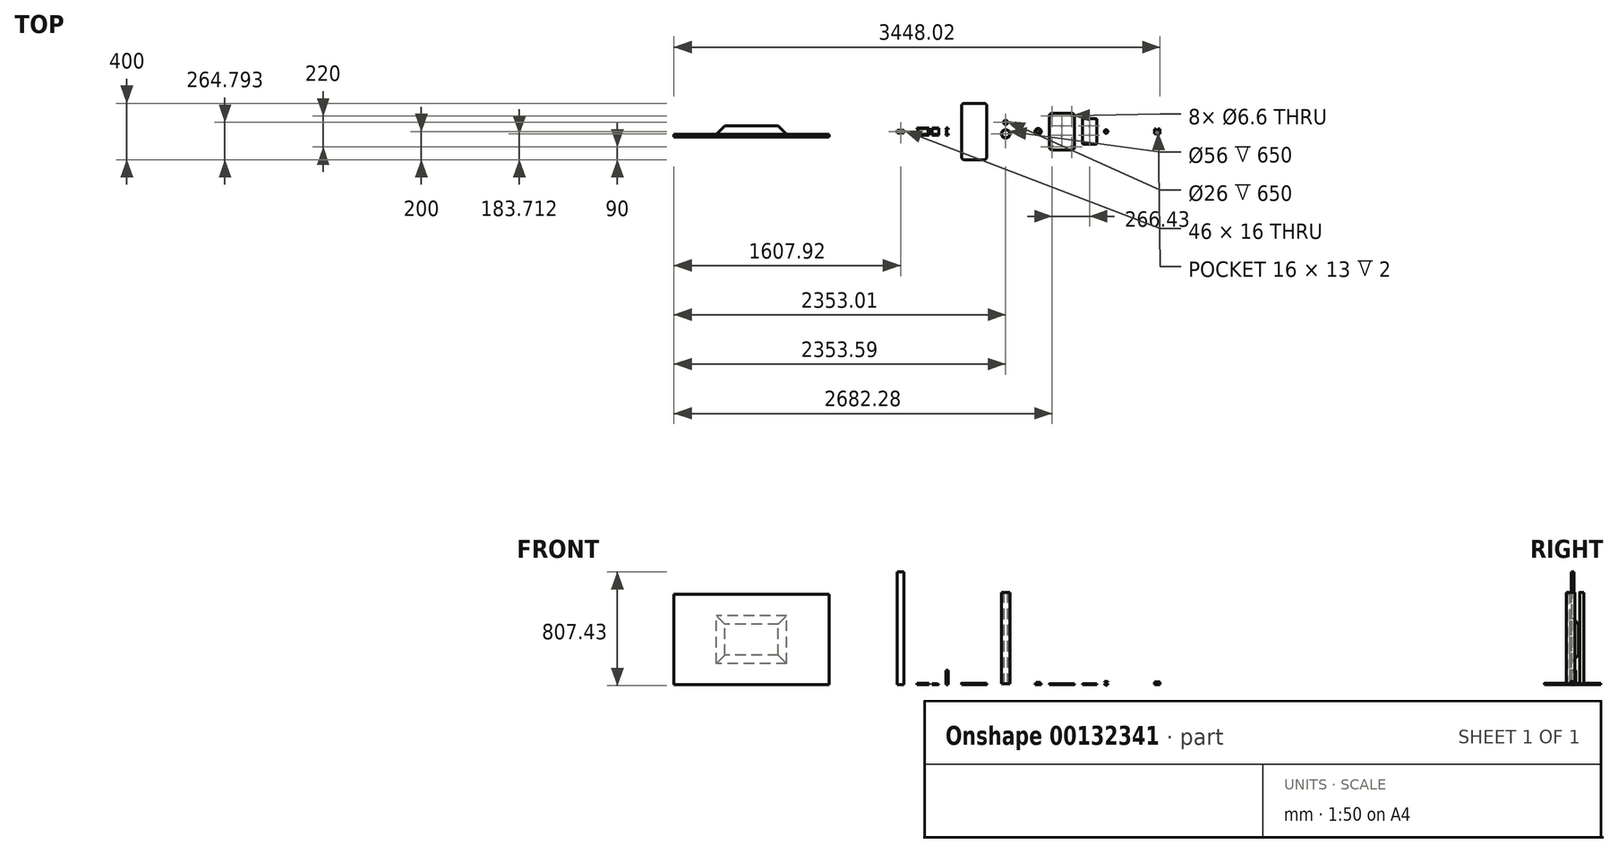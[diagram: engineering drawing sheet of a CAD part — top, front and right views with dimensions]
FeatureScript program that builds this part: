
annotation { "Feature Type Name" : "Feature", "Feature Type Description" : "" }
export const myFeature = defineFeature(function(context is Context, id is Id, definition is map)
    precondition{}
    {
        {
            var Q0;
            Q0=qCreatedBy(makeId("Top.planeOp"),FACE);
            var sketch = newSketch(context, id + "F0", { "sketchPlane" : qUnion([Q0])});
            skLineSegment(sketch, "E0.bottom", {"start": v(78.82, 130) * mm, "end": v(258.82, 130) * mm});
            skLineSegment(sketch, "E0.top", {"start": v(78.82, -130) * mm, "end": v(258.82, -130) * mm});
            skLineSegment(sketch, "E0.left", {"start": v(78.82, 130) * mm, "end": v(78.82, -130) * mm});
            skLineSegment(sketch, "E0.right", {"start": v(258.82, 130) * mm, "end": v(258.82, -130) * mm});
            skPoint(sketch, "E0.middle", {"position": v(0, 0) * mm});
            skSolve(sketch);
        }
        {
            var Q0;
            Q0 = qSketchRegion(id + "F0", true);
            extrude(context, id + "F1", {"entities" : qUnion([Q0]), "depth" : 5 * mm});
        }
        {
            var Q0;
            Q0=makeQuery(id+"F1.opExtrude","CAP_FACE",FACE,{"disambiguationData":[OSD([sQuery(id+"F0.wireOp",EDGE,"E0.bottom"),sQuery(id+"F0.wireOp",EDGE,"E0.top"),sQuery(id+"F0.wireOp",EDGE,"E0.left"),sQuery(id+"F0.wireOp",EDGE,"E0.right")])],"isStart":false});
            var sketch = newSketch(context, id + "F2", { "sketchPlane" : qUnion([Q0])});
            skArc(sketch, "E1", {"start": v(98.82, 130) * mm, "mid": v(84.67, 124.14) * mm, "end": v(78.82, 110) * mm});
            skLineSegment(sketch, "E2", {"start": v(98.82, 130) * mm, "end": v(78.82, 130) * mm});
            skLineSegment(sketch, "E3", {"start": v(78.82, 130) * mm, "end": v(78.82, 110) * mm});
            skLineSegment(sketch, "E4", {"start": v(258.82, 130) * mm, "end": v(238.82, 130) * mm});
            skLineSegment(sketch, "E5", {"start": v(258.82, 130) * mm, "end": v(258.82, 110) * mm});
            skArc(sketch, "E6", {"start": v(258.82, 110) * mm, "mid": v(252.96, 124.14) * mm, "end": v(238.82, 130) * mm});
            skLineSegment(sketch, "E7", {"start": v(98.82, -130) * mm, "end": v(78.82, -130) * mm});
            skLineSegment(sketch, "E8", {"start": v(78.82, -130) * mm, "end": v(78.82, -110) * mm});
            skLineSegment(sketch, "E9", {"start": v(238.82, -130) * mm, "end": v(258.82, -130) * mm});
            skLineSegment(sketch, "E10", {"start": v(258.82, -130) * mm, "end": v(258.82, -110) * mm});
            skArc(sketch, "E11", {"start": v(238.82, -130) * mm, "mid": v(252.96, -124.14) * mm, "end": v(258.82, -110) * mm});
            skArc(sketch, "E12", {"start": v(78.82, -110) * mm, "mid": v(84.67, -124.14) * mm, "end": v(98.82, -130) * mm});
            skSolve(sketch);
        }
        {
            var Q0;
            Q0 = qSketchRegion(id + "F2", true);
            extrude(context, id + "F3", {"entities" : qUnion([Q0]), "operationType" : NewBodyOperationType.REMOVE, "endBound" : BoundingType.THROUGH_ALL, "oppositeDirection" : true, "depth" : 25 * mm});
        }
        {
            var Q0;
            Q0=makeQuery(id+"F1.opExtrude","CAP_FACE",FACE,{"disambiguationData":[OSD([sQuery(id+"F0.wireOp",EDGE,"E0.bottom"),sQuery(id+"F0.wireOp",EDGE,"E0.top"),sQuery(id+"F0.wireOp",EDGE,"E0.left"),sQuery(id+"F0.wireOp",EDGE,"E0.right")])],"isStart":false});
            var sketch = newSketch(context, id + "F4", { "sketchPlane" : qUnion([Q0])});
            skPoint(sketch, "E13", {"position": v(98.82, 110) * mm});
            skPoint(sketch, "E14", {"position": v(238.82, 110) * mm});
            skPoint(sketch, "E15", {"position": v(98.82, -110) * mm});
            skPoint(sketch, "E16", {"position": v(238.82, -110) * mm});
            skPoint(sketch, "E17", {"position": v(0, 40) * mm});
            skPoint(sketch, "E18", {"position": v(0, -25) * mm});
            skPoint(sketch, "E19", {"position": v(168.82, 40) * mm});
            skPoint(sketch, "E19.positionSnap0", {"position": v(168.82, 130) * mm});
            skPoint(sketch, "E20", {"position": v(168.82, -25) * mm});
            skSolve(sketch);
        }
        {
            var Q0;
            Q0=sQuery(id+"F4.wireOp",VERTEX,"E13");
            var Q1;
            Q1=sQuery(id+"F4.wireOp",VERTEX,"E14");
            var Q2;
            Q2=sQuery(id+"F4.wireOp",VERTEX,"E17");
            var Q3;
            Q3=sQuery(id+"F4.wireOp",VERTEX,"E18");
            var Q4;
            Q4=sQuery(id+"F4.wireOp",VERTEX,"E15");
            var Q5;
            Q5=sQuery(id+"F4.wireOp",VERTEX,"E16");
            var Q6;
            Q6=sQuery(id+"F4.wireOp",VERTEX,"E19");
            var Q7;
            Q7=sQuery(id+"F4.wireOp",VERTEX,"E20");
            var Q8;
            Q8=makeQuery(id+"F1.opExtrude","SWEPT_BODY",BODY,{"disambiguationData":[OSD([sQuery(id+"F0.wireOp",EDGE,"E0.bottom"),sQuery(id+"F0.wireOp",EDGE,"E0.top"),sQuery(id+"F0.wireOp",EDGE,"E0.left"),sQuery(id+"F0.wireOp",EDGE,"E0.right")])]});
            hole(context, id + "F5", {"style" : HoleStyle.SIMPLE, "endStyle" : HoleEndStyle.THROUGH, "standardTappedOrClearance" : lookupTablePath({ "standard" : "ISO", "fit" : "Normal", "size" : "M6", "type" : "Clearance" }), "standardBlindInLast" : lookupTablePath({ "fit" : "Standard", "standard" : "ISO", "size" : "M6", "type" : "Clearance" }), "holeDiameter" : 6.6 * mm, "majorDiameter" : 5 * mm, "locations" : qUnion([Q0, Q1, Q2, Q3, Q4, Q5, Q6, Q7]), "scope" : qUnion([Q8]), "isTappedThrough" : true, "tappedDepth" : 12 * mm, "tapClearance" : 3});
        }
        {
            var Q0;
            Q0=qCreatedBy(makeId("Top.planeOp"),FACE);
            var sketch = newSketch(context, id + "F6", { "sketchPlane" : qUnion([Q0])});
            skLineSegment(sketch, "E21.bottom", {"start": v(415.25, -90) * mm, "end": v(315.25, -90) * mm});
            skLineSegment(sketch, "E21.top", {"start": v(415.25, 90) * mm, "end": v(315.25, 90) * mm});
            skLineSegment(sketch, "E21.left", {"start": v(415.25, -90) * mm, "end": v(415.25, 90) * mm});
            skLineSegment(sketch, "E21.right", {"start": v(315.25, -90) * mm, "end": v(315.25, 90) * mm});
            skPoint(sketch, "E21.middle", {"position": v(365.25, 0) * mm});
            skSolve(sketch);
        }
        {
            var Q0;
            Q0 = qSketchRegion(id + "F6", true);
            extrude(context, id + "F7", {"entities" : qUnion([Q0]), "depth" : 5 * mm});
        }
        {
            var Q0;
            Q0=makeQuery(id+"F7.opExtrude","CAP_FACE",FACE,{"disambiguationData":[OSD([sQuery(id+"F6.wireOp",EDGE,"E21.bottom"),sQuery(id+"F6.wireOp",EDGE,"E21.top"),sQuery(id+"F6.wireOp",EDGE,"E21.left"),sQuery(id+"F6.wireOp",EDGE,"E21.right")])],"isStart":false});
            var sketch = newSketch(context, id + "F8", { "sketchPlane" : qUnion([Q0])});
            skArc(sketch, "E22", {"start": v(320.25, 90) * mm, "mid": v(316.71, 88.54) * mm, "end": v(315.25, 85) * mm});
            skLineSegment(sketch, "E23", {"start": v(320.25, 90) * mm, "end": v(315.25, 90) * mm});
            skArc(sketch, "E24", {"start": v(415.25, 85) * mm, "mid": v(413.78, 88.54) * mm, "end": v(410.25, 90) * mm});
            skLineSegment(sketch, "E25", {"start": v(410.25, 90) * mm, "end": v(415.25, 90) * mm});
            skLineSegment(sketch, "E26", {"start": v(415.25, 90) * mm, "end": v(415.25, 85) * mm});
            skArc(sketch, "E27", {"start": v(315.25, -85) * mm, "mid": v(316.71, -88.54) * mm, "end": v(320.25, -90) * mm});
            skLineSegment(sketch, "E28", {"start": v(315.25, -85) * mm, "end": v(315.25, -90) * mm});
            skLineSegment(sketch, "E29", {"start": v(315.25, -90) * mm, "end": v(320.25, -90) * mm});
            skArc(sketch, "E30", {"start": v(410.25, -90) * mm, "mid": v(413.78, -88.54) * mm, "end": v(415.25, -85) * mm});
            skLineSegment(sketch, "E31", {"start": v(415.25, -85) * mm, "end": v(415.25, -90) * mm});
            skLineSegment(sketch, "E32", {"start": v(415.25, -90) * mm, "end": v(410.25, -90) * mm});
            skLineSegment(sketch, "E33", {"start": v(315.25, 90) * mm, "end": v(315.25, 85) * mm});
            skSolve(sketch);
        }
        {
            var Q0;
            Q0 = qSketchRegion(id + "F8", true);
            extrude(context, id + "F9", {"entities" : qUnion([Q0]), "operationType" : NewBodyOperationType.REMOVE, "endBound" : BoundingType.THROUGH_ALL, "oppositeDirection" : true, "depth" : 25 * mm});
        }
        {
            var Q0;
            Q0=makeQuery(id+"F7.opExtrude","CAP_FACE",FACE,{"disambiguationData":[OSD([sQuery(id+"F6.wireOp",EDGE,"E21.bottom"),sQuery(id+"F6.wireOp",EDGE,"E21.top"),sQuery(id+"F6.wireOp",EDGE,"E21.left"),sQuery(id+"F6.wireOp",EDGE,"E21.right")])],"isStart":false});
            var sketch = newSketch(context, id + "F10", { "sketchPlane" : qUnion([Q0])});
            skPoint(sketch, "E34", {"position": v(365.25, 40) * mm});
            skPoint(sketch, "E34.positionSnap0", {"position": v(365.25, 90) * mm});
            skPoint(sketch, "E35", {"position": v(365.25, -25) * mm});
            skSolve(sketch);
        }
        {
            var Q0;
            Q0=sQuery(id+"F10.wireOp",VERTEX,"E34");
            var Q1;
            Q1=sQuery(id+"F10.wireOp",VERTEX,"E35");
            var Q2;
            Q2=makeQuery(id+"F7.opExtrude","SWEPT_BODY",BODY,{"disambiguationData":[OSD([sQuery(id+"F6.wireOp",EDGE,"E21.bottom"),sQuery(id+"F6.wireOp",EDGE,"E21.top"),sQuery(id+"F6.wireOp",EDGE,"E21.left"),sQuery(id+"F6.wireOp",EDGE,"E21.right")])]});
            hole(context, id + "F11", {"style" : HoleStyle.SIMPLE, "endStyle" : HoleEndStyle.THROUGH, "standardTappedOrClearance" : lookupTablePath({ "standard" : "ISO", "fit" : "Normal", "size" : "M6", "type" : "Clearance" }), "standardBlindInLast" : lookupTablePath({ "fit" : "Standard", "standard" : "ISO", "size" : "M6", "type" : "Clearance" }), "holeDiameter" : 6.6 * mm, "majorDiameter" : 5 * mm, "locations" : qUnion([Q0, Q1]), "scope" : qUnion([Q2]), "isTappedThrough" : true, "tappedDepth" : 12 * mm, "tapClearance" : 3});
        }
        {
            var Q0;
            Q0=makeQuery(id+"F7.opExtrude","CAP_FACE",FACE,{"disambiguationData":[OSD([sQuery(id+"F6.wireOp",EDGE,"E21.bottom"),sQuery(id+"F6.wireOp",EDGE,"E21.top"),sQuery(id+"F6.wireOp",EDGE,"E21.left"),sQuery(id+"F6.wireOp",EDGE,"E21.right")])],"isStart":false});
            var sketch = newSketch(context, id + "F12", { "sketchPlane" : qUnion([Q0])});
            skCircle(sketch, "E36", {"center": v(-229.87, -16.29) * mm, "radius": 28 * mm});
            skCircle(sketch, "E37", {"center": v(-229.87, -16.29) * mm, "radius": 30 * mm});
            skCircle(sketch, "E38", {"center": v(-230.45, 64.8) * mm, "radius": 13 * mm});
            skCircle(sketch, "E39", {"center": v(-230.45, 64.8) * mm, "radius": 15 * mm});
            skSolve(sketch);
        }
        {
            var Q0;
            Q0 = qSketchRegion(id + "F12", true);
            extrude(context, id + "F13", {"entities" : qUnion([Q0]), "depth" : 650 * mm});
        }
        {
            var Q0;
            Q0=qCreatedBy(makeId("Front.planeOp"),FACE);
            var sketch = newSketch(context, id + "F14", { "sketchPlane" : qUnion([Q0])});
            skLineSegment(sketch, "E40", {"start": v(469.57, 22.57) * mm, "end": v(469.57, 17.57) * mm});
            skLineSegment(sketch, "E41", {"start": v(469.57, 17.57) * mm, "end": v(479.57, 17.57) * mm});
            skLineSegment(sketch, "E42", {"start": v(479.57, 17.57) * mm, "end": v(479.57, 7.57) * mm});
            skLineSegment(sketch, "E43", {"start": v(479.57, 7.57) * mm, "end": v(469.57, 7.57) * mm});
            skLineSegment(sketch, "E44", {"start": v(469.57, 7.57) * mm, "end": v(469.57, 2.57) * mm});
            skLineSegment(sketch, "E45", {"start": v(469.57, 22.57) * mm, "end": v(482.07, 22.57) * mm});
            skLineSegment(sketch, "E46", {"start": v(469.57, 2.57) * mm, "end": v(482.07, -7.43) * mm});
            skLineSegment(sketch, "E47", {"start": v(482.07, 22.57) * mm, "end": v(482.07, -7.43) * mm, "construction": true});
            skLineSegment(sketch, "E48", {"start": v(482.07, 22.57) * mm, "end": v(482.07, -7.43) * mm});
            skSolve(sketch);
        }
        {
            var Q0;
            Q0 = qSketchRegion(id + "F14", true);
            var Q1;
            Q1=sQuery(id+"F14.wireOp",EDGE,"E47");
            revolve(context, id + "F15", {"entities" : qUnion([Q0]), "axis" : qUnion([Q1]), "revolveType" : RevolveType.FULL});
        }
        {
            var Q0;
            Q0=qCreatedBy(makeId("Top.planeOp"),FACE);
            var sketch = newSketch(context, id + "F16", { "sketchPlane" : qUnion([Q0])});
            skLineSegment(sketch, "E49.bottom", {"start": v(-523.6, 200) * mm, "end": v(-383.6, 200) * mm});
            skLineSegment(sketch, "E49.top", {"start": v(-523.6, -200) * mm, "end": v(-383.6, -200) * mm});
            skLineSegment(sketch, "E49.left", {"start": v(-543.6, 180) * mm, "end": v(-543.6, -180) * mm});
            skLineSegment(sketch, "E49.right", {"start": v(-363.6, 180) * mm, "end": v(-363.6, -180) * mm});
            skPoint(sketch, "E49.middle", {"position": v(-453.6, 0) * mm});
            skPoint(sketch, "E50.visualSharp", {"position": v(-543.6, 200) * mm});
            skArc(sketch, "E50.filletArc", {"start": v(-523.6, 200) * mm, "mid": v(-537.75, 194.14) * mm, "end": v(-543.6, 180) * mm});
            skPoint(sketch, "E51.visualSharp", {"position": v(-363.6, 200) * mm});
            skArc(sketch, "E51.filletArc", {"start": v(-363.6, 180) * mm, "mid": v(-369.46, 194.14) * mm, "end": v(-383.6, 200) * mm});
            skPoint(sketch, "E52.visualSharp", {"position": v(-363.6, -200) * mm});
            skArc(sketch, "E52.filletArc", {"start": v(-383.6, -200) * mm, "mid": v(-369.46, -194.14) * mm, "end": v(-363.6, -180) * mm});
            skPoint(sketch, "E53.visualSharp", {"position": v(-543.6, -200) * mm});
            skArc(sketch, "E53.filletArc", {"start": v(-543.6, -180) * mm, "mid": v(-537.75, -194.14) * mm, "end": v(-523.6, -200) * mm});
            skSolve(sketch);
        }
        {
            var Q0;
            Q0 = qSketchRegion(id + "F16", true);
            extrude(context, id + "F17", {"entities" : qUnion([Q0]), "depth" : 10 * mm});
        }
        {
            var Q0;
            Q0=qCreatedBy(makeId("Top.planeOp"),FACE);
            var sketch = newSketch(context, id + "F18", { "sketchPlane" : qUnion([Q0])});
            skLineSegment(sketch, "E54.bottom", {"start": v(-654.7, 25) * mm, "end": v(-639.2, 25) * mm});
            skLineSegment(sketch, "E54.top", {"start": v(-654.7, -25) * mm, "end": v(-639.2, -25) * mm});
            skLineSegment(sketch, "E54.left", {"start": v(-654.7, 25) * mm, "end": v(-654.7, -25) * mm});
            skLineSegment(sketch, "E54.right", {"start": v(-639.2, 25) * mm, "end": v(-639.2, -25) * mm});
            skPoint(sketch, "E54.middle", {"position": v(-646.94, 0) * mm});
            skSolve(sketch);
        }
        {
            var Q0;
            Q0 = qSketchRegion(id + "F18", true);
            extrude(context, id + "F19", {"entities" : qUnion([Q0]), "depth" : 100 * mm});
        }
        {
            var Q0;
            Q0=makeQuery(id+"F19.opExtrude","SWEPT_FACE",FACE,{"disambiguationData":[OSD([sQuery(id+"F18.wireOp",EDGE,"E54.left")])]});
            var sketch = newSketch(context, id + "F20", { "sketchPlane" : qUnion([Q0])});
            skLineSegment(sketch, "E55.bottom", {"start": v(25, 100) * mm, "end": v(22.75, 100) * mm});
            skLineSegment(sketch, "E55.top", {"start": v(25, 10) * mm, "end": v(22.75, 10) * mm});
            skLineSegment(sketch, "E55.left", {"start": v(25, 100) * mm, "end": v(25, 10) * mm});
            skLineSegment(sketch, "E55.right", {"start": v(22.75, 100) * mm, "end": v(22.75, 10) * mm});
            skLineSegment(sketch, "E56.bottom", {"start": v(-25, 100) * mm, "end": v(-22.75, 100) * mm});
            skLineSegment(sketch, "E56.top", {"start": v(-25, 10) * mm, "end": v(-22.75, 10) * mm});
            skLineSegment(sketch, "E56.left", {"start": v(-25, 100) * mm, "end": v(-25, 10) * mm});
            skLineSegment(sketch, "E56.right", {"start": v(-22.75, 100) * mm, "end": v(-22.75, 10) * mm});
            skSolve(sketch);
        }
        {
            var Q0;
            Q0 = qSketchRegion(id + "F20", true);
            extrude(context, id + "F21", {"entities" : qUnion([Q0]), "operationType" : NewBodyOperationType.REMOVE, "endBound" : BoundingType.UP_TO_NEXT, "oppositeDirection" : true, "depth" : 25 * mm});
        }
        {
            var Q0;
            Q0=makeQuery(id+"F19.opExtrude","CAP_FACE",FACE,{"disambiguationData":[OSD([sQuery(id+"F18.wireOp",EDGE,"E54.bottom"),sQuery(id+"F18.wireOp",EDGE,"E54.top"),sQuery(id+"F18.wireOp",EDGE,"E54.left"),sQuery(id+"F18.wireOp",EDGE,"E54.right")])],"isStart":false});
            var sketch = newSketch(context, id + "F22", { "sketchPlane" : qUnion([Q0])});
            skLineSegment(sketch, "E57.bottom", {"start": v(-654.7, 20.25) * mm, "end": v(-649.7, 20.25) * mm});
            skLineSegment(sketch, "E57.top", {"start": v(-654.7, -20.25) * mm, "end": v(-649.7, -20.25) * mm});
            skLineSegment(sketch, "E57.left", {"start": v(-654.7, 20.25) * mm, "end": v(-654.7, -20.25) * mm});
            skLineSegment(sketch, "E57.right", {"start": v(-649.7, 20.25) * mm, "end": v(-649.7, -20.25) * mm});
            skPoint(sketch, "E57.middle", {"position": v(-652.2, 0) * mm});
            skPoint(sketch, "E57.middle.positionSnap0", {"position": v(-654.7, 0) * mm});
            skPoint(sketch, "E57.centerSnap0", {"position": v(-654.7, 0) * mm});
            skSolve(sketch);
        }
        {
            var Q0;
            Q0 = qSketchRegion(id + "F22", true);
            extrude(context, id + "F23", {"entities" : qUnion([Q0]), "operationType" : NewBodyOperationType.REMOVE, "endBound" : BoundingType.UP_TO_NEXT, "oppositeDirection" : true, "depth" : 25 * mm});
        }
        {
            var Q0;
            Q0=makeQuery(id+"F19.opExtrude","CAP_FACE",FACE,{"disambiguationData":[OSD([sQuery(id+"F18.wireOp",EDGE,"E54.bottom"),sQuery(id+"F18.wireOp",EDGE,"E54.top"),sQuery(id+"F18.wireOp",EDGE,"E54.left"),sQuery(id+"F18.wireOp",EDGE,"E54.right")])],"isStart":false});
            var sketch = newSketch(context, id + "F24", { "sketchPlane" : qUnion([Q0])});
            skLineSegment(sketch, "E58.bottom", {"start": v(-639.2, 15) * mm, "end": v(-644.2, 15) * mm});
            skLineSegment(sketch, "E58.top", {"start": v(-639.2, -15) * mm, "end": v(-644.2, -15) * mm});
            skLineSegment(sketch, "E58.left", {"start": v(-639.2, 15) * mm, "end": v(-639.2, -15) * mm});
            skLineSegment(sketch, "E58.right", {"start": v(-646.2, 13) * mm, "end": v(-646.2, -13) * mm});
            skPoint(sketch, "E58.middle", {"position": v(-642.7, 0) * mm});
            skPoint(sketch, "E58.middle.positionSnap0", {"position": v(-639.2, 0) * mm});
            skPoint(sketch, "E58.centerSnap0", {"position": v(-639.2, 0) * mm});
            skPoint(sketch, "E59.visualSharp", {"position": v(-646.2, 15) * mm});
            skArc(sketch, "E59.filletArc", {"start": v(-644.2, 15) * mm, "mid": v(-645.6, 14.41) * mm, "end": v(-646.2, 13) * mm});
            skPoint(sketch, "E60.visualSharp", {"position": v(-646.2, -15) * mm});
            skArc(sketch, "E60.filletArc", {"start": v(-646.2, -13) * mm, "mid": v(-645.6, -14.41) * mm, "end": v(-644.2, -15) * mm});
            skSolve(sketch);
        }
        {
            var Q0;
            Q0 = qSketchRegion(id + "F24", true);
            extrude(context, id + "F25", {"entities" : qUnion([Q0]), "operationType" : NewBodyOperationType.REMOVE, "endBound" : BoundingType.UP_TO_NEXT, "oppositeDirection" : true, "depth" : 25 * mm});
        }
        {
            var Q0;
            Q0=qCreatedBy(makeId("Top.planeOp"),FACE);
            var sketch = newSketch(context, id + "F26", { "sketchPlane" : qUnion([Q0])});
            skLineSegment(sketch, "E61.bottom", {"start": v(-859.9, -25) * mm, "end": v(-774.9, -25) * mm});
            skLineSegment(sketch, "E61.top", {"start": v(-859.9, 25) * mm, "end": v(-774.9, 25) * mm});
            skLineSegment(sketch, "E61.left", {"start": v(-859.9, -25) * mm, "end": v(-859.9, 25) * mm});
            skLineSegment(sketch, "E61.right", {"start": v(-774.9, -25) * mm, "end": v(-774.9, 25) * mm});
            skPoint(sketch, "E61.middle", {"position": v(-817.4, 0) * mm});
            skSolve(sketch);
        }
        {
            var Q0;
            Q0 = qSketchRegion(id + "F26", true);
            extrude(context, id + "F27", {"entities" : qUnion([Q0]), "depth" : 8 * mm});
        }
        {
            var Q0;
            Q0=makeQuery(id+"F27.opExtrude","SWEPT_FACE",FACE,{"disambiguationData":[OSD([sQuery(id+"F26.wireOp",EDGE,"E61.left")])]});
            var sketch = newSketch(context, id + "F28", { "sketchPlane" : qUnion([Q0])});
            skLineSegment(sketch, "E62.bottom", {"start": v(-20.25, 8) * mm, "end": v(20.25, 8) * mm});
            skLineSegment(sketch, "E62.top", {"start": v(-20.25, 2) * mm, "end": v(20.25, 2) * mm});
            skLineSegment(sketch, "E62.left", {"start": v(-20.25, 8) * mm, "end": v(-20.25, 2) * mm});
            skLineSegment(sketch, "E62.right", {"start": v(20.25, 8) * mm, "end": v(20.25, 2) * mm});
            skPoint(sketch, "E62.middle", {"position": v(0, 5) * mm});
            skSolve(sketch);
        }
        {
            var Q0;
            Q0 = qSketchRegion(id + "F28", true);
            extrude(context, id + "F29", {"entities" : qUnion([Q0]), "operationType" : NewBodyOperationType.REMOVE, "oppositeDirection" : true, "depth" : 80 * mm});
        }
        {
            var Q0;
            Q0=makeQuery(id+"F27.opExtrude","CAP_FACE",FACE,{"disambiguationData":[OSD([sQuery(id+"F26.wireOp",EDGE,"E61.bottom"),sQuery(id+"F26.wireOp",EDGE,"E61.top"),sQuery(id+"F26.wireOp",EDGE,"E61.left"),sQuery(id+"F26.wireOp",EDGE,"E61.right")])],"isStart":true});
            var sketch = newSketch(context, id + "F30", { "sketchPlane" : qUnion([Q0])});
            skLineSegment(sketch, "E63.bottom", {"start": v(-859.9, 20.25) * mm, "end": v(-854.9, 20.25) * mm});
            skLineSegment(sketch, "E63.top", {"start": v(-859.9, -20.25) * mm, "end": v(-854.9, -20.25) * mm});
            skLineSegment(sketch, "E63.left", {"start": v(-859.9, 20.25) * mm, "end": v(-859.9, -20.25) * mm});
            skLineSegment(sketch, "E63.right", {"start": v(-854.9, 20.25) * mm, "end": v(-854.9, -20.25) * mm});
            skPoint(sketch, "E63.middle", {"position": v(-857.4, 0) * mm});
            skPoint(sketch, "E63.middle.positionSnap0", {"position": v(-859.9, 0) * mm});
            skPoint(sketch, "E63.centerSnap0", {"position": v(-859.9, 0) * mm});
            skSolve(sketch);
        }
        {
            var Q0;
            Q0 = qSketchRegion(id + "F30", true);
            extrude(context, id + "F31", {"entities" : qUnion([Q0]), "operationType" : NewBodyOperationType.REMOVE, "oppositeDirection" : true, "depth" : 8 * mm});
        }
        {
            var Q0;
            {var subQ1=sQuery(id+"F28.wireOp",EDGE,"E62.left");var subQ2=sQuery(id+"F28.wireOp",EDGE,"E62.top");Q0=makeQuery(id+"F31.boolean.opBoolean","INTERSECT",EDGE,{"derivedFrom":[makeQuery(id+"FVbMaS613Q0wGzE_8.boolean.opBoolean","SPLIT",FACE,{"disambiguationData":[TD([makeQuery(id+"F29.boolean.opBoolean","COPY",FACE,{"derivedFrom":makeQuery(id+"F29.opExtrude","SWEPT_FACE",FACE,{"disambiguationData":[OSD([subQ1])]})})])],"derivedFrom":makeQuery(id+"F29.boolean.opBoolean","COPY",FACE,{"derivedFrom":makeQuery(id+"F29.opExtrude","SWEPT_FACE",FACE,{"disambiguationData":[OSD([subQ2])]})})}),makeQuery(id+"F31.opExtrude","SWEPT_FACE",FACE,{"disambiguationData":[OSD([sQuery(id+"F30.wireOp",EDGE,"E63.right")])]})]});}
            fillet(context, id + "F32", {"entities" : qUnion([Q0]), "radius" : 3 * mm, "tangentPropagation" : true, "allowEdgeOverflow" : false});
        }
        {
            var Q0;
            Q0=qCreatedBy(makeId("Top.planeOp"),FACE);
            var sketch = newSketch(context, id + "F33", { "sketchPlane" : qUnion([Q0])});
            skLineSegment(sketch, "E64.bottom", {"start": v(-752.17, 25) * mm, "end": v(-705.17, 25) * mm});
            skLineSegment(sketch, "E64.top", {"start": v(-752.17, -25) * mm, "end": v(-705.17, -25) * mm});
            skLineSegment(sketch, "E64.left", {"start": v(-752.17, 25) * mm, "end": v(-752.17, -25) * mm});
            skLineSegment(sketch, "E64.right", {"start": v(-705.17, 25) * mm, "end": v(-705.17, -25) * mm});
            skPoint(sketch, "E64.middle", {"position": v(-728.67, 0) * mm});
            skSolve(sketch);
        }
        {
            var Q0;
            Q0 = qSketchRegion(id + "F33", true);
            extrude(context, id + "F34", {"entities" : qUnion([Q0]), "depth" : 7 * mm});
        }
        {
            var Q0;
            Q0=makeQuery(id+"F34.opExtrude","CAP_FACE",FACE,{"disambiguationData":[OSD([sQuery(id+"F33.wireOp",EDGE,"E64.bottom"),sQuery(id+"F33.wireOp",EDGE,"E64.top"),sQuery(id+"F33.wireOp",EDGE,"E64.left"),sQuery(id+"F33.wireOp",EDGE,"E64.right")])],"isStart":false});
            var sketch = newSketch(context, id + "F35", { "sketchPlane" : qUnion([Q0])});
            skLineSegment(sketch, "E65.bottom", {"start": v(-752.17, 20.25) * mm, "end": v(-716.17, 20.25) * mm});
            skLineSegment(sketch, "E65.top", {"start": v(-752.17, -20.25) * mm, "end": v(-716.17, -20.25) * mm});
            skLineSegment(sketch, "E65.left", {"start": v(-752.17, 20.25) * mm, "end": v(-752.17, -20.25) * mm});
            skLineSegment(sketch, "E65.right", {"start": v(-716.17, 20.25) * mm, "end": v(-716.17, -20.25) * mm});
            skPoint(sketch, "E65.middle", {"position": v(-734.17, 0) * mm});
            skSolve(sketch);
        }
        {
            var Q0;
            Q0 = qSketchRegion(id + "F35", true);
            extrude(context, id + "F36", {"entities" : qUnion([Q0]), "operationType" : NewBodyOperationType.REMOVE, "oppositeDirection" : true, "depth" : 5 * mm});
        }
        {
            var Q0;
            Q0=makeQuery(id+"F23.boolean.opBoolean","COPY",FACE,{"derivedFrom":makeQuery(id+"F23.opExtrude","SWEPT_FACE",FACE,{"disambiguationData":[OSD([sQuery(id+"F22.wireOp",EDGE,"E57.right")])]})});
            var sketch = newSketch(context, id + "F37", { "sketchPlane" : qUnion([Q0])});
            skCircle(sketch, "E66", {"center": v(-10, 91) * mm, "radius": 2.75 * mm});
            skCircle(sketch, "E67", {"center": v(10, 41) * mm, "radius": 2.75 * mm});
            skSolve(sketch);
        }
        {
            var Q0;
            Q0 = qSketchRegion(id + "F37", true);
            extrude(context, id + "F38", {"entities" : qUnion([Q0]), "operationType" : NewBodyOperationType.REMOVE, "endBound" : BoundingType.UP_TO_NEXT, "oppositeDirection" : true, "depth" : 25 * mm});
        }
        {
            var Q0;
            {var subQ0=sQuery(id+"F18.wireOp",EDGE,"E54.top");var subQ1=sQuery(id+"F18.wireOp",EDGE,"E54.right");Q0=makeQuery(id+"F25.boolean.opBoolean","SPLIT",FACE,{"disambiguationData":[TD([makeQuery(id+"F19.opExtrude","SWEPT_FACE",FACE,{"disambiguationData":[OSD([subQ0])]})])],"derivedFrom":makeQuery(id+"F19.opExtrude","SWEPT_FACE",FACE,{"disambiguationData":[OSD([subQ1])]})});}
            var sketch = newSketch(context, id + "F39", { "sketchPlane" : qUnion([Q0])});
            skLineSegment(sketch, "E68.left", {"start": v(-14, 37) * mm, "end": v(-14, 45) * mm});
            skLineSegment(sketch, "E68.right", {"start": v(-6, 37) * mm, "end": v(-6, 45) * mm});
            skPoint(sketch, "E68.middle", {"position": v(-10, 41) * mm});
            skLineSegment(sketch, "E69.left", {"start": v(6, 87) * mm, "end": v(6, 95) * mm});
            skLineSegment(sketch, "E69.right", {"start": v(14, 87) * mm, "end": v(14, 95) * mm});
            skPoint(sketch, "E69.middle", {"position": v(10, 91) * mm});
            skLineSegment(sketch, "E70", {"start": v(-14, 45) * mm, "end": v(-10, 45.9) * mm});
            skLineSegment(sketch, "E71", {"start": v(-14, 37) * mm, "end": v(-10, 36.1) * mm});
            skLineSegment(sketch, "E72", {"start": v(-10, 45.9) * mm, "end": v(-6, 45) * mm});
            skLineSegment(sketch, "E73", {"start": v(-6, 37) * mm, "end": v(-10, 36.1) * mm});
            skLineSegment(sketch, "E74", {"start": v(6, 95) * mm, "end": v(10, 95.9) * mm});
            skLineSegment(sketch, "E75", {"start": v(10, 95.9) * mm, "end": v(14, 95) * mm});
            skLineSegment(sketch, "E76", {"start": v(6, 87) * mm, "end": v(10, 86.1) * mm});
            skLineSegment(sketch, "E77", {"start": v(10, 86.1) * mm, "end": v(14, 87) * mm});
            skSolve(sketch);
        }
        {
            var Q0;
            Q0 = qSketchRegion(id + "F39", true);
            extrude(context, id + "F40", {"entities" : qUnion([Q0]), "operationType" : NewBodyOperationType.REMOVE, "oppositeDirection" : true, "depth" : 8.5 * mm});
        }
        {
            var Q0;
            Q0=makeQuery(id+"F34.opExtrude","CAP_FACE",FACE,{"disambiguationData":[OSD([sQuery(id+"F33.wireOp",EDGE,"E64.bottom"),sQuery(id+"F33.wireOp",EDGE,"E64.top"),sQuery(id+"F33.wireOp",EDGE,"E64.left"),sQuery(id+"F33.wireOp",EDGE,"E64.right")])],"isStart":false});
            var sketch = newSketch(context, id + "F41", { "sketchPlane" : qUnion([Q0])});
            skLineSegment(sketch, "E78.bottom", {"start": v(-705.17, 25) * mm, "end": v(-716.17, 25) * mm});
            skLineSegment(sketch, "E78.top", {"start": v(-705.17, -25) * mm, "end": v(-716.17, -25) * mm});
            skLineSegment(sketch, "E78.left", {"start": v(-705.17, 25) * mm, "end": v(-705.17, -25) * mm});
            skLineSegment(sketch, "E78.right", {"start": v(-716.17, 25) * mm, "end": v(-716.17, -25) * mm});
            skSolve(sketch);
        }
        {
            var Q0;
            Q0 = qSketchRegion(id + "F41", true);
            extrude(context, id + "F42", {"entities" : qUnion([Q0]), "operationType" : NewBodyOperationType.REMOVE, "oppositeDirection" : true, "depth" : 5 * mm});
        }
        {
            var Q0;
            Q0=qCreatedBy(makeId("Top.planeOp"),FACE);
            var sketch = newSketch(context, id + "F43", { "sketchPlane" : qUnion([Q0])});
            skCircle(sketch, "E79", {"center": v(0, 0) * mm, "radius": 22 * mm});
            skSolve(sketch);
        }
        {
            var Q0;
            Q0=makeQuery(id+"F43.imprint","IMPRINT",FACE,{"disambiguationData":[TD([[makeQuery(id+"F43.imprint","IMPRINT",EDGE,{"derivedFrom":sQuery(id+"F43.wireOp",EDGE,"E79")}),1.0]])]});
            extrude(context, id + "F44", {"entities" : qUnion([Q0]), "depth" : 15 * mm});
        }
        {
            var Q0;
            Q0=qCreatedBy(makeId("Front.planeOp"),FACE);
            var sketch = newSketch(context, id + "F45", { "sketchPlane" : qUnion([Q0])});
            skLineSegment(sketch, "E80", {"start": v(22, 15) * mm, "end": v(15, 15) * mm});
            skLineSegment(sketch, "E81", {"start": v(22, 15) * mm, "end": v(22, 5) * mm});
            skLineSegment(sketch, "E82", {"start": v(22, 5) * mm, "end": v(17, 6) * mm});
            skLineSegment(sketch, "E83", {"start": v(17, 6) * mm, "end": v(15, 15) * mm});
            skLineSegment(sketch, "E84", {"start": v(0, 26.42) * mm, "end": v(0, -3.58) * mm, "construction": true});
            skSolve(sketch);
        }
        {
            var Q0;
            Q0 = qSketchRegion(id + "F45", true);
            var Q1;
            Q1=sQuery(id+"F45.wireOp",EDGE,"E84");
            revolve(context, id + "F46", {"operationType" : NewBodyOperationType.REMOVE, "entities" : qUnion([Q0]), "axis" : qUnion([Q1]), "revolveType" : RevolveType.FULL, "oppositeDirection" : true});
        }
        {
            var Q0;
            Q0=qCreatedBy(makeId("Front.planeOp"),FACE);
            var sketch = newSketch(context, id + "F47", { "sketchPlane" : qUnion([Q0])});
            skLineSegment(sketch, "E85", {"start": v(-22, 5) * mm, "end": v(-22, 4.5) * mm});
            skLineSegment(sketch, "E86", {"start": v(-22, 5) * mm, "end": v(-17.02, 6) * mm});
            skLineSegment(sketch, "E87", {"start": v(-17.02, 6) * mm, "end": v(-15.01, 15) * mm});
            skLineSegment(sketch, "E88", {"start": v(-15.01, 15) * mm, "end": v(-7.01, 15) * mm});
            skLineSegment(sketch, "E89", {"start": v(-7.01, 15) * mm, "end": v(-7.01, 14.5) * mm});
            skLineSegment(sketch, "E90", {"start": v(-7.01, 14.5) * mm, "end": v(-14.5, 14.5) * mm});
            skLineSegment(sketch, "E91", {"start": v(-14.5, 14.5) * mm, "end": v(-16.5, 5.6) * mm});
            skLineSegment(sketch, "E92", {"start": v(-16.5, 5.6) * mm, "end": v(-22, 4.5) * mm});
            skSolve(sketch);
        }
        {
            var Q0;
            Q0 = qSketchRegion(id + "F47", true);
            extrude(context, id + "F48", {"entities" : qUnion([Q0]), "operationType" : NewBodyOperationType.REMOVE, "oppositeDirection" : true, "depth" : 0.75 * mm, "hasSecondDirection" : true, "secondDirectionOppositeDirection" : false, "secondDirectionDepth" : 0.75 * mm});
        }
        {
            var Q0;
            Q0=makeQuery(id+"F44.opExtrude","CAP_FACE",FACE,{"disambiguationData":[OSD([sQuery(id+"F43.wireOp",EDGE,"E79")])],"isStart":true});
            var sketch = newSketch(context, id + "F49", { "sketchPlane" : qUnion([Q0])});
            skArc(sketch, "E93", {"start": v(-2, 2.24) * mm, "mid": v(3, 0) * mm, "end": v(-2, -2.24) * mm});
            skLineSegment(sketch, "E94", {"start": v(-2, 2.24) * mm, "end": v(-2, -2.24) * mm});
            skSolve(sketch);
        }
        {
            var Q0;
            Q0 = qSketchRegion(id + "F49", true);
            extrude(context, id + "F50", {"entities" : qUnion([Q0]), "operationType" : NewBodyOperationType.REMOVE, "oppositeDirection" : true, "depth" : 12 * mm});
        }
        {
            var Q0;
            Q0=qCreatedBy(makeId("Top.planeOp"),FACE);
            var sketch = newSketch(context, id + "F51", { "sketchPlane" : qUnion([Q0])});
            skLineSegment(sketch, "E95.bottom", {"start": v(824.56, -18) * mm, "end": v(864.56, -18) * mm});
            skLineSegment(sketch, "E95.top", {"start": v(824.56, 18) * mm, "end": v(864.56, 18) * mm});
            skLineSegment(sketch, "E95.left", {"start": v(824.56, -18) * mm, "end": v(824.56, 18) * mm});
            skLineSegment(sketch, "E95.right", {"start": v(864.56, -18) * mm, "end": v(864.56, 18) * mm});
            skPoint(sketch, "E95.middle", {"position": v(844.56, 0) * mm});
            skSolve(sketch);
        }
        {
            var Q0;
            Q0 = qSketchRegion(id + "F51", true);
            extrude(context, id + "F52", {"entities" : qUnion([Q0]), "depth" : 20 * mm});
        }
        {
            var Q0;
            Q0=makeQuery(id+"F52.opExtrude","CAP_FACE",FACE,{"disambiguationData":[OSD([sQuery(id+"F51.wireOp",EDGE,"E95.bottom"),sQuery(id+"F51.wireOp",EDGE,"E95.top"),sQuery(id+"F51.wireOp",EDGE,"E95.left"),sQuery(id+"F51.wireOp",EDGE,"E95.right")])],"isStart":false});
            var sketch = newSketch(context, id + "F53", { "sketchPlane" : qUnion([Q0])});
            skLineSegment(sketch, "E96.bottom", {"start": v(824.56, 18) * mm, "end": v(864.56, 18) * mm});
            skLineSegment(sketch, "E96.top", {"start": v(824.56, -13) * mm, "end": v(864.56, -13) * mm});
            skLineSegment(sketch, "E96.left", {"start": v(824.56, 18) * mm, "end": v(824.56, -13) * mm});
            skLineSegment(sketch, "E96.right", {"start": v(864.56, 18) * mm, "end": v(864.56, -13) * mm});
            skSolve(sketch);
        }
        {
            var Q0;
            Q0 = qSketchRegion(id + "F53", true);
            extrude(context, id + "F54", {"entities" : qUnion([Q0]), "operationType" : NewBodyOperationType.REMOVE, "oppositeDirection" : true, "depth" : 10 * mm});
        }
        {
            var Q0;
            Q0=makeQuery(id+"F54.boolean.opBoolean","COPY",FACE,{"derivedFrom":makeQuery(id+"F54.opExtrude","CAP_FACE",FACE,{"disambiguationData":[OSD([sQuery(id+"F53.wireOp",EDGE,"E96.bottom"),sQuery(id+"F53.wireOp",EDGE,"E96.top"),sQuery(id+"F53.wireOp",EDGE,"E96.left"),sQuery(id+"F53.wireOp",EDGE,"E96.right")])],"isStart":false})});
            var sketch = newSketch(context, id + "F55", { "sketchPlane" : qUnion([Q0])});
            skLineSegment(sketch, "E97.bottom", {"start": v(836.56, -13) * mm, "end": v(852.56, -13) * mm});
            skLineSegment(sketch, "E97.top", {"start": v(836.56, 13) * mm, "end": v(852.56, 13) * mm});
            skLineSegment(sketch, "E97.left", {"start": v(836.56, -13) * mm, "end": v(836.56, 13) * mm});
            skLineSegment(sketch, "E97.right", {"start": v(852.56, -13) * mm, "end": v(852.56, 13) * mm});
            skSolve(sketch);
        }
        {
            var Q0;
            Q0 = qSketchRegion(id + "F55", true);
            extrude(context, id + "F56", {"entities" : qUnion([Q0]), "operationType" : NewBodyOperationType.REMOVE, "oppositeDirection" : true, "depth" : 5 * mm});
        }
        {
            var Q0;
            Q0=makeQuery(id+"F56.boolean.opBoolean","COPY",FACE,{"derivedFrom":makeQuery(id+"F56.opExtrude","CAP_FACE",FACE,{"disambiguationData":[OSD([sQuery(id+"F55.wireOp",EDGE,"E97.bottom"),sQuery(id+"F55.wireOp",EDGE,"E97.top"),sQuery(id+"F55.wireOp",EDGE,"E97.left"),sQuery(id+"F55.wireOp",EDGE,"E97.right")])],"isStart":false})});
            var sketch = newSketch(context, id + "F57", { "sketchPlane" : qUnion([Q0])});
            skLineSegment(sketch, "E98.bottom", {"start": v(836.56, -13) * mm, "end": v(852.56, -13) * mm});
            skLineSegment(sketch, "E98.top", {"start": v(836.56, 0) * mm, "end": v(852.56, 0) * mm});
            skLineSegment(sketch, "E98.left", {"start": v(836.56, -13) * mm, "end": v(836.56, 0) * mm});
            skLineSegment(sketch, "E98.right", {"start": v(852.56, -13) * mm, "end": v(852.56, 0) * mm});
            skSolve(sketch);
        }
        {
            var Q0;
            Q0 = qSketchRegion(id + "F57", true);
            extrude(context, id + "F58", {"entities" : qUnion([Q0]), "operationType" : NewBodyOperationType.REMOVE, "oppositeDirection" : true, "depth" : 2 * mm});
        }
        {
            var Q0;
            Q0=makeQuery(id+"F54.boolean.opBoolean","COPY",FACE,{"derivedFrom":makeQuery(id+"F54.opExtrude","CAP_FACE",FACE,{"disambiguationData":[OSD([sQuery(id+"F53.wireOp",EDGE,"E96.bottom"),sQuery(id+"F53.wireOp",EDGE,"E96.top"),sQuery(id+"F53.wireOp",EDGE,"E96.left"),sQuery(id+"F53.wireOp",EDGE,"E96.right")])],"isStart":false})});
            var sketch = newSketch(context, id + "F59", { "sketchPlane" : qUnion([Q0])});
            skLineSegment(sketch, "E99.bottom", {"start": v(836.56, 13) * mm, "end": v(852.56, 13) * mm});
            skLineSegment(sketch, "E99.top", {"start": v(836.56, 18) * mm, "end": v(852.56, 18) * mm});
            skLineSegment(sketch, "E99.left", {"start": v(836.56, 13) * mm, "end": v(836.56, 18) * mm});
            skLineSegment(sketch, "E99.right", {"start": v(852.56, 13) * mm, "end": v(852.56, 18) * mm});
            skSolve(sketch);
        }
        {
            var Q0;
            Q0 = qSketchRegion(id + "F59", true);
            extrude(context, id + "F60", {"entities" : qUnion([Q0]), "operationType" : NewBodyOperationType.REMOVE, "oppositeDirection" : true, "depth" : 20 * mm});
        }
        {
            var Q0;
            Q0=makeQuery(id+"F52.opExtrude","CAP_FACE",FACE,{"disambiguationData":[OSD([sQuery(id+"F51.wireOp",EDGE,"E95.bottom"),sQuery(id+"F51.wireOp",EDGE,"E95.top"),sQuery(id+"F51.wireOp",EDGE,"E95.left"),sQuery(id+"F51.wireOp",EDGE,"E95.right")])],"isStart":true});
            var sketch = newSketch(context, id + "F61", { "sketchPlane" : qUnion([Q0])});
            skLineSegment(sketch, "E100.bottom", {"start": v(824.56, -18) * mm, "end": v(836.56, -18) * mm});
            skLineSegment(sketch, "E100.top", {"start": v(824.56, -13) * mm, "end": v(836.56, -13) * mm});
            skLineSegment(sketch, "E100.left", {"start": v(824.56, -18) * mm, "end": v(824.56, -13) * mm});
            skLineSegment(sketch, "E100.right", {"start": v(836.56, -18) * mm, "end": v(836.56, -13) * mm});
            skLineSegment(sketch, "E101.bottom", {"start": v(864.56, -18) * mm, "end": v(852.56, -18) * mm});
            skLineSegment(sketch, "E101.top", {"start": v(864.56, -13) * mm, "end": v(852.56, -13) * mm});
            skLineSegment(sketch, "E101.left", {"start": v(864.56, -18) * mm, "end": v(864.56, -13) * mm});
            skLineSegment(sketch, "E101.right", {"start": v(852.56, -18) * mm, "end": v(852.56, -13) * mm});
            skSolve(sketch);
        }
        {
            var Q0;
            Q0 = qSketchRegion(id + "F61", true);
            extrude(context, id + "F62", {"entities" : qUnion([Q0]), "operationType" : NewBodyOperationType.REMOVE, "oppositeDirection" : true, "depth" : 5 * mm});
        }
        {
            var Q0;
            Q0=qCreatedBy(makeId("Top.planeOp"),FACE);
            var sketch = newSketch(context, id + "F63", { "sketchPlane" : qUnion([Q0])});
            skLineSegment(sketch, "E102.bottom", {"start": v(-1000.54, -10) * mm, "end": v(-950.54, -10) * mm});
            skLineSegment(sketch, "E102.top", {"start": v(-1000.54, 10) * mm, "end": v(-950.54, 10) * mm});
            skLineSegment(sketch, "E102.left", {"start": v(-1000.54, -10) * mm, "end": v(-1000.54, 10) * mm});
            skLineSegment(sketch, "E102.right", {"start": v(-950.54, -10) * mm, "end": v(-950.54, 10) * mm});
            skPoint(sketch, "E102.middle", {"position": v(-975.54, 0) * mm});
            skLineSegment(sketch, "E103.bottom", {"start": v(-998.54, -8) * mm, "end": v(-952.54, -8) * mm});
            skLineSegment(sketch, "E103.top", {"start": v(-998.54, 8) * mm, "end": v(-952.54, 8) * mm});
            skLineSegment(sketch, "E103.left", {"start": v(-998.54, -8) * mm, "end": v(-998.54, 8) * mm});
            skLineSegment(sketch, "E103.right", {"start": v(-952.54, -8) * mm, "end": v(-952.54, 8) * mm});
            skSolve(sketch);
        }
        {
            var Q0;
            Q0 = qSketchRegion(id + "F63", true);
            extrude(context, id + "F64", {"entities" : qUnion([Q0]), "depth" : 800 * mm});
        }
        {
            var Q0;
            Q0=qCreatedBy(makeId("Top.planeOp"),FACE);
            var sketch = newSketch(context, id + "F65", { "sketchPlane" : qUnion([Q0])});
            skLineSegment(sketch, "E104.bottom", {"start": v(-1483.46, -40) * mm, "end": v(-2583.46, -40) * mm});
            skLineSegment(sketch, "E104.top", {"start": v(-1483.46, 40) * mm, "end": v(-2583.46, 40) * mm});
            skLineSegment(sketch, "E104.left", {"start": v(-1483.46, -40) * mm, "end": v(-1483.46, 40) * mm});
            skLineSegment(sketch, "E104.right", {"start": v(-2583.46, -40) * mm, "end": v(-2583.46, 40) * mm});
            skPoint(sketch, "E104.middle", {"position": v(-2033.46, 0) * mm});
            skSolve(sketch);
        }
        {
            var Q0;
            Q0 = qSketchRegion(id + "F65", true);
            extrude(context, id + "F66", {"entities" : qUnion([Q0]), "depth" : 640 * mm});
        }
        {
            var Q0;
            Q0=makeQuery(id+"F66.opExtrude","CAP_FACE",FACE,{"disambiguationData":[OSD([sQuery(id+"F65.wireOp",EDGE,"E104.bottom"),sQuery(id+"F65.wireOp",EDGE,"E104.top"),sQuery(id+"F65.wireOp",EDGE,"E104.left"),sQuery(id+"F65.wireOp",EDGE,"E104.right")])],"isStart":false});
            var sketch = newSketch(context, id + "F67", { "sketchPlane" : qUnion([Q0])});
            skLineSegment(sketch, "E105", {"start": v(-2583.46, 40) * mm, "end": v(-2583.46, -20) * mm});
            skLineSegment(sketch, "E106", {"start": v(-2583.46, -20) * mm, "end": v(-2283.46, -20) * mm});
            skLineSegment(sketch, "E107", {"start": v(-1483.46, 40) * mm, "end": v(-1483.46, -20) * mm});
            skLineSegment(sketch, "E108", {"start": v(-1483.46, -20) * mm, "end": v(-1783.46, -20) * mm});
            skLineSegment(sketch, "E109", {"start": v(-1783.46, -20) * mm, "end": v(-1843.46, 40) * mm});
            skLineSegment(sketch, "E110", {"start": v(-2283.46, -20) * mm, "end": v(-2223.46, 40) * mm});
            skLineSegment(sketch, "E111", {"start": v(-2583.46, 40) * mm, "end": v(-2223.46, 40) * mm});
            skLineSegment(sketch, "E112", {"start": v(-1843.46, 40) * mm, "end": v(-1483.46, 40) * mm});
            skSolve(sketch);
        }
        {
            var Q0;
            Q0=makeQuery(id+"F66.opExtrude","SWEPT_FACE",FACE,{"disambiguationData":[OSD([sQuery(id+"F65.wireOp",EDGE,"E104.right")])]});
            var sketch = newSketch(context, id + "F68", { "sketchPlane" : qUnion([Q0])});
            skLineSegment(sketch, "E113", {"start": v(-40, 640) * mm, "end": v(20, 640) * mm});
            skLineSegment(sketch, "E114", {"start": v(20, 640) * mm, "end": v(20, 490) * mm});
            skLineSegment(sketch, "E115", {"start": v(20, 490) * mm, "end": v(-40, 430) * mm});
            skLineSegment(sketch, "E116", {"start": v(-40, 430) * mm, "end": v(-40, 640) * mm});
            skLineSegment(sketch, "E117", {"start": v(-40, 0) * mm, "end": v(20, 0) * mm});
            skLineSegment(sketch, "E118", {"start": v(20, 0) * mm, "end": v(20, 150) * mm});
            skLineSegment(sketch, "E119", {"start": v(20, 150) * mm, "end": v(-40, 210) * mm});
            skLineSegment(sketch, "E120", {"start": v(-40, 210) * mm, "end": v(-40, 0) * mm});
            skSolve(sketch);
        }
        {
            var Q0;
            Q0 = qSketchRegion(id + "F67", true);
            extrude(context, id + "F69", {"entities" : qUnion([Q0]), "operationType" : NewBodyOperationType.REMOVE, "oppositeDirection" : true, "depth" : 640 * mm});
        }
        {
            var Q0;
            Q0 = qSketchRegion(id + "F68", true);
            extrude(context, id + "F70", {"entities" : qUnion([Q0]), "operationType" : NewBodyOperationType.REMOVE, "oppositeDirection" : true, "depth" : 1100 * mm});
        }
    });
